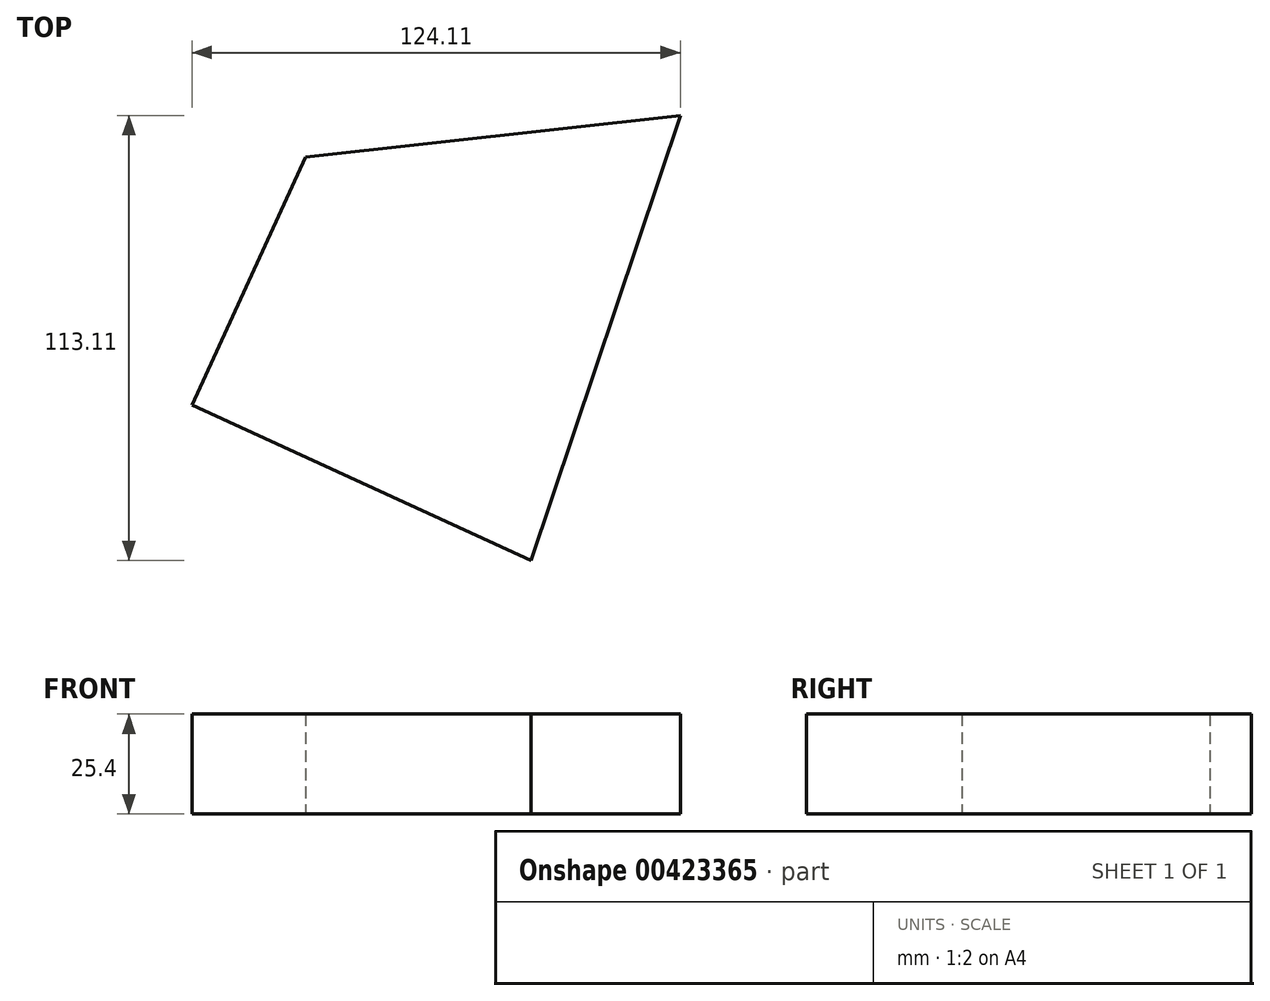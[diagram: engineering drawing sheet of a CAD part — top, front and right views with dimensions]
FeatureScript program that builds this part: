
annotation { "Feature Type Name" : "Feature", "Feature Type Description" : "" }
export const myFeature = defineFeature(function(context is Context, id is Id, definition is map)
    precondition{}
    {
        {
            var Q0;
            Q0=qCreatedBy(makeId("Top.planeOp"),FACE);
            var sketch = newSketch(context, id + "F0", { "sketchPlane" : qUnion([Q0])});
            skLineSegment(sketch, "E0", {"start": v(72.74, 73.57) * mm, "end": v(34.74, -39.54) * mm});
            skLineSegment(sketch, "E1", {"start": v(34.74, -39.54) * mm, "end": v(-51.37, 0) * mm});
            skLineSegment(sketch, "E2", {"start": v(-51.37, 0) * mm, "end": v(-22.47, 62.93) * mm});
            skLineSegment(sketch, "E3", {"start": v(-22.47, 62.93) * mm, "end": v(72.74, 73.57) * mm});
            skSolve(sketch);
        }
        {
            var Q0;
            Q0=makeQuery(id+"F0.imprint","IMPRINT",FACE,{"disambiguationData":[TD([[makeQuery(id+"F0.imprint","IMPRINT",EDGE,{"derivedFrom":sQuery(id+"F0.wireOp",EDGE,"E0")}),-1.0]])]});
            extrude(context, id + "F1", {"entities" : qUnion([Q0]), "depth" : 25.4 * mm});
        }
    });
